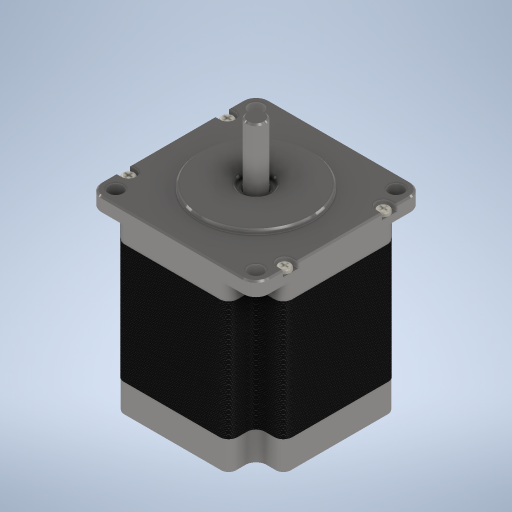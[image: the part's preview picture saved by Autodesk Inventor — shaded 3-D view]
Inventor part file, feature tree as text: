
AUTODESK INVENTOR PART (.ipt)
format: ipt  version: 2023 (Build 270158000, 158)  size: 3,253,248 bytes
history: native  units: mm
features: sketch x15, extrude x12, fillet x4, chamfer x4, projected_geometry x2, plane x1, sweep x1
ambient origin geometry x8: Origin, YZ Plane, XZ Plane, XY Plane, X Axis, Y Axis, Z Axis, Center Point
bodies: Solid1 (feature_tree)
feature tree (39):
  extrude  "Extrusion1"  Depth=38.0mm
  extrude  "Extrusion2"  Depth=28.2mm
  extrude  "Extrusion3"  Depth=10.0mm TaperAngle=0.0deg
  extrude  "Extrusion4"  Depth=40.0mm TaperAngle=0.0deg
  extrude  "Extrusion5"  Depth=56.4mm
  extrude  "Extrusion6"  Depth=5.0mm TaperAngle=0.0deg
  extrude  "Extrusion7"  Depth=1.6mm TaperAngle=0.0deg
  extrude  "Extrusion8"  Depth=1.6mm TaperAngle=0.0deg
  fillet  "Fillet1"  Radius=6.65mm
  extrude  "Extrusion9"  Depth=26.0mm
  fillet  "Fillet2"  Radius=26.0mm
  chamfer  "Chamfer1"  Distance=26.0mm
  chamfer  "Chamfer2"  Distance=2.0mm Angle=45.0deg
  chamfer  "Chamfer4"  Distance=2.0mm Angle=45.0deg
  extrude  "Extrusion10"  Depth=5.0mm
  extrude  "Extrusion11"  Depth=2.5mm
  fillet  "Fillet3"  Radius=2.0mm
  extrude  "Extrusion12"  Depth=2.0mm
  fillet  "Fillet4"  Radius=1.25mm
  sketch  "Sketch13"  dims[d44=4.65mm d45=0.5mm d46=2.0mm d47=45.0deg d48=0.5mm d49=2.0mm d50=45.0deg]
  plane  "Work Plane1"
  sweep  "Sweep1"
  chamfer  "Chamfer5"  Distance=2.5mm
  sketch  "Sketch1"  dims[d7=56.4mm d8=38.0mm]
  sketch  "Sketch2"  dims[d9=28.2mm d10=28.2mm]
  projected_geometry  "Projected Loop1"
  sketch  "Sketch3"  dims[d12=38.0mm d13=10.0mm d14=0.0mm]
  projected_geometry  "Projected Loop2"
  sketch  "Sketch4"  dims[d15=0.1mm d16=40.0mm d17=0.0mm]
  sketch  "Sketch5"  dims[d18=5.0mm d19=0.0mm d20=56.4mm]
  sketch  "Sketch6"  dims[d21=56.4mm d22=5.0mm d23=0.0mm]
  sketch  "Sketch7"  dims[d24=38.0mm d25=1.6mm d26=0.0mm]
  sketch  "Sketch8"  dims[d27=10.0mm d28=1.6mm d29=0.0mm d30=6.65mm]
  sketch  "Sketch9"  dims[d31=5.0mm d32=0.0mm d33=6.35mm d34=26.0mm d35=0.0mm]
  sketch  "Sketch10"  dims[d36=3.0mm]
  sketch  "Sketch11"  dims[d40=47.1mm]
  sketch  "Sketch12"  dims[d41=5.0mm d42=26.0mm d43=0.0mm]
  sketch  "Sketch14"  dims[d54=0.5mm d55=2.0mm d56=45.0deg d57=5.0mm d58=2.5mm d60=2.0mm d61=0.0mm d62=4.0mm d63=1.25mm d64=0.0mm d65=0.6mm d66=2.5mm d67=2.5mm d68=0.4mm d69=1.25mm d70=1.25mm d71=1.0mm d72=0.0mm d73=0.3mm d75=0.0mm d76=0.15mm d77=0.519615mm d78=770.0mm d80=0.519615mm d81=10.0mm d83=10.0mm d85=0.519615mm d86=770.0mm d88=0.519615mm d89=10.0mm d91=10.0mm d93=0.0mm d94=0.0mm d95=0.5mm d96=2.0mm d97=45.0deg]
  sketch  "3D Sketch1"
